# Revit family: DR3 FAMILIA 2026
name_source: partatom
category: Terminales de aire
units: mm (PartAtom-declared; Revit-internal decimal feet)

## family parameters
Compartido = No
Corte con vacíos al cargar = No
Cota de conector redondo = Usar diámetro
Mantener orientación de anotación = No
Punto de cálculo de habitación = No
Se basa en plano de trabajo = No
Siempre vertical = Sí
Tipo de pieza = Normal

## types (11) — shared parameters
zero-valued in all types: Elevación por defecto

## per-type parameters (varying)
| type | DIAM | RAD IN | RAD MID | RADIO |
| 6 | 6 " | 2 " | 5 " | 7 " |
| 8 | 8 " | 3 " | 6 " | 8 " |
| 10 | 10 " | 3 " | 6 " | 9 " |
| 12 | 12 " | 3 " | 7 " | 10 " |
| 14 | 16 " | 4 " | 9 " | 12 " |
| 16 | 16 " | 4 " | 9 " | 12 " |
| 18 | 18 " | 4 " | 9 " | 13 " |
| 24 | 24 " | 5 " | 12 " | 16 " |
| 20 | 20 " | 5 " | 10 " | 14 " |
| 30 | 30 " | 6 " | 14 " | 19 " |
| 36 | 36 " | 7 " | 16 " | 22 " |

## geometry (parser evidence)
native form markers: Sweep x8
no freeform markers — native parametric forms only
